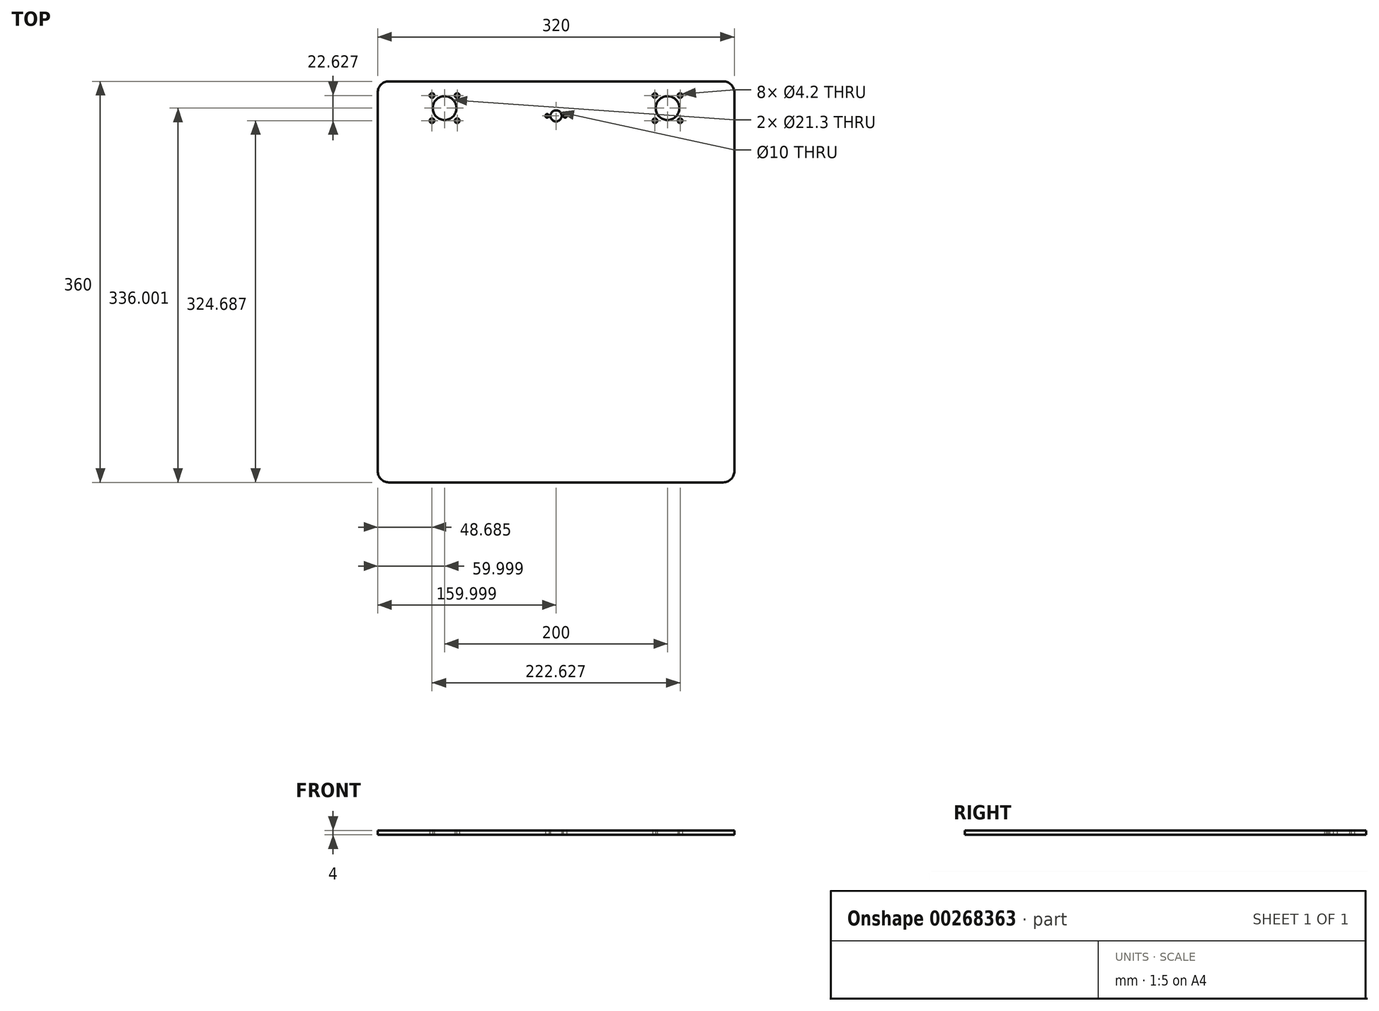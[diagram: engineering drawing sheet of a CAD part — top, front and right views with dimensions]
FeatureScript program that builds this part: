
annotation { "Feature Type Name" : "Feature", "Feature Type Description" : "" }
export const myFeature = defineFeature(function(context is Context, id is Id, definition is map)
    precondition{}
    {
        {
            var Q0;
            Q0=qCreatedBy(makeId("Top.planeOp"),FACE);
            var sketch = newSketch(context, id + "F0", { "sketchPlane" : qUnion([Q0])});
            skLineSegment(sketch, "E0.bottom", {"start": v(-144, 157.92) * mm, "end": v(156, 157.92) * mm});
            skLineSegment(sketch, "E0.top", {"start": v(-144, -202.08) * mm, "end": v(156, -202.08) * mm});
            skLineSegment(sketch, "E0.left", {"start": v(-154, 147.92) * mm, "end": v(-154, -192.08) * mm});
            skLineSegment(sketch, "E0.right", {"start": v(166, 147.92) * mm, "end": v(166, -192.08) * mm});
            skLineSegment(sketch, "E1", {"start": v(6, 157.92) * mm, "end": v(6, -202.08) * mm, "construction": true});
            skCircle(sketch, "E2", {"center": v(-94, 133.92) * mm, "radius": 10.65 * mm});
            skCircle(sketch, "E3", {"center": v(106, 133.92) * mm, "radius": 10.65 * mm});
            skCircle(sketch, "E4", {"center": v(6, 126.92) * mm, "radius": 5 * mm});
            skCircle(sketch, "E5", {"center": v(106, 133.92) * mm, "radius": 16 * mm, "construction": true});
            skCircle(sketch, "E6", {"center": v(94.69, 145.23) * mm, "radius": 2.1 * mm});
            skCircle(sketch, "E7", {"center": v(117.31, 145.23) * mm, "radius": 2.1 * mm});
            skCircle(sketch, "E8", {"center": v(117.31, 122.6) * mm, "radius": 2.1 * mm});
            skCircle(sketch, "E9", {"center": v(94.69, 122.6) * mm, "radius": 2.1 * mm});
            skLineSegment(sketch, "E10", {"start": v(106, 133.92) * mm, "end": v(106, 149.92) * mm, "construction": true});
            skLineSegment(sketch, "E11", {"start": v(106, 133.92) * mm, "end": v(94.69, 145.23) * mm, "construction": true});
            skCircle(sketch, "E12", {"center": v(-94, 133.92) * mm, "radius": 16 * mm, "construction": true});
            skCircle(sketch, "E13", {"center": v(-105.31, 145.23) * mm, "radius": 2.1 * mm});
            skCircle(sketch, "E14", {"center": v(-82.69, 145.23) * mm, "radius": 2.1 * mm});
            skCircle(sketch, "E15", {"center": v(-82.69, 122.6) * mm, "radius": 2.1 * mm});
            skCircle(sketch, "E16", {"center": v(-105.31, 122.6) * mm, "radius": 2.1 * mm});
            skLineSegment(sketch, "E17", {"start": v(-94, 133.92) * mm, "end": v(-94, 149.92) * mm, "construction": true});
            skLineSegment(sketch, "E18", {"start": v(-94, 133.92) * mm, "end": v(-105.31, 145.23) * mm, "construction": true});
            skLineSegment(sketch, "E19", {"start": v(-2.7, 126.92) * mm, "end": v(14.9, 126.92) * mm, "construction": true});
            skCircle(sketch, "E20", {"center": v(14, 126.92) * mm, "radius": 1.6 * mm});
            skCircle(sketch, "E21", {"center": v(-2, 126.92) * mm, "radius": 1.6 * mm});
            skPoint(sketch, "E22.visualSharp", {"position": v(-154, 157.92) * mm});
            skArc(sketch, "E22.filletArc", {"start": v(-144, 157.92) * mm, "mid": v(-151.07, 155) * mm, "end": v(-154, 147.92) * mm});
            skPoint(sketch, "E23.visualSharp", {"position": v(166, 157.92) * mm});
            skArc(sketch, "E23.filletArc", {"start": v(166, 147.92) * mm, "mid": v(163.07, 155) * mm, "end": v(156, 157.92) * mm});
            skPoint(sketch, "E24.visualSharp", {"position": v(166, -202.08) * mm});
            skArc(sketch, "E24.filletArc", {"start": v(156, -202.08) * mm, "mid": v(163.07, -199.15) * mm, "end": v(166, -192.08) * mm});
            skPoint(sketch, "E25.visualSharp", {"position": v(-154, -202.08) * mm});
            skArc(sketch, "E25.filletArc", {"start": v(-154, -192.08) * mm, "mid": v(-151.07, -199.15) * mm, "end": v(-144, -202.08) * mm});
            skSolve(sketch);
        }
        {
            var Q0;
            Q0=qSketchRegion(id+"F0",true);
            extrude(context, id + "F1", {"entities" : qUnion([Q0]), "depth" : 4 * mm});
        }
    });
